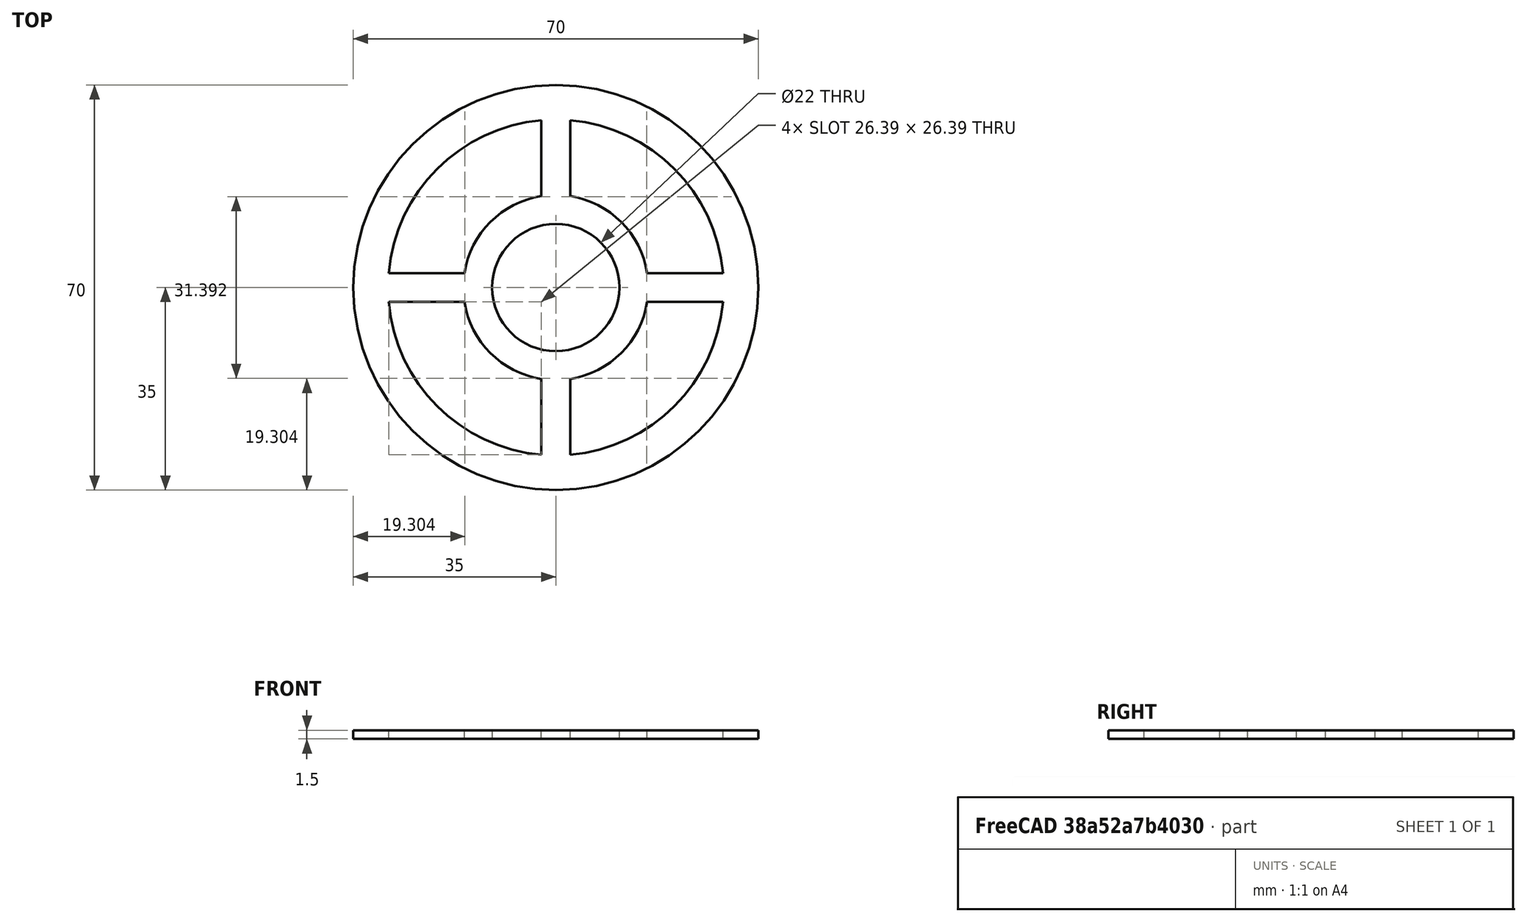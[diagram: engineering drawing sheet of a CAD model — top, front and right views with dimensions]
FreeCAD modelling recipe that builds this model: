
FCSTD DOCUMENT  (FreeCAD 0.14R3700 (Git))
Label: BR_PCB_bas
License: CC-BY 3.0
LicenseURL: http://creativecommons.org/licenses/by/3.0/
objects: Sketcher::SketchObject×1, Part::Extrusion×1, Part::Feature×1
note: 3 computed .brp shape members not serialized (recipe doc carries the construction recipe); baked Part::Feature solids carry a one-line shape summary decoded from their .brp

FEATURE [Sketcher::SketchObject] Sketch  label="PCB_bas"
  sketch-geometry (18):
    g0: Circle CenterX=0 CenterY=0 CenterZ=0 NormalX=0 NormalY=0 NormalZ=1 Radius=35
    g1: Circle CenterX=0 CenterY=0 CenterZ=0 NormalX=0 NormalY=0 NormalZ=1 Radius=11
    g2: ArcOfCircle CenterX=0 CenterY=0 CenterZ=0 NormalX=0 NormalY=0 NormalZ=1 Radius=16 StartAngle=1.72769 EndAngle=2.9847
    g3: ArcOfCircle CenterX=0 CenterY=0 CenterZ=0 NormalX=0 NormalY=0 NormalZ=1 Radius=29 StartAngle=1.65711 EndAngle=3.05528
    g4: LineSegment StartX=-28.892 StartY=2.5 StartZ=0 EndX=-15.8035 EndY=2.5 EndZ=0
    g5: LineSegment StartX=-2.5 StartY=28.892 StartZ=0 EndX=-2.5 EndY=15.8035 EndZ=0
    g6: ArcOfCircle CenterX=0 CenterY=0 CenterZ=0 NormalX=0 NormalY=0 NormalZ=1 Radius=16 StartAngle=0.156893 EndAngle=1.4139
    g7: ArcOfCircle CenterX=0 CenterY=0 CenterZ=0 NormalX=0 NormalY=0 NormalZ=1 Radius=29 StartAngle=0.086314 EndAngle=1.48448
    g8: ArcOfCircle CenterX=0 CenterY=0 CenterZ=0 NormalX=0 NormalY=0 NormalZ=1 Radius=16 StartAngle=4.86928 EndAngle=6.12629
    g9: ArcOfCircle CenterX=0 CenterY=0 CenterZ=0 NormalX=0 NormalY=0 NormalZ=1 Radius=29 StartAngle=4.7987 EndAngle=6.19687
    g10: ArcOfCircle CenterX=0 CenterY=0 CenterZ=0 NormalX=0 NormalY=0 NormalZ=1 Radius=16 StartAngle=3.29849 EndAngle=4.5555
    g11: ArcOfCircle CenterX=0 CenterY=0 CenterZ=0 NormalX=0 NormalY=0 NormalZ=1 Radius=29 StartAngle=3.22791 EndAngle=4.62607
    g12: LineSegment StartX=2.5 StartY=15.8035 StartZ=0 EndX=2.5 EndY=28.892 EndZ=0
    g13: LineSegment StartX=15.8035 StartY=2.5 StartZ=0 EndX=28.892 EndY=2.5 EndZ=0
    g14: LineSegment StartX=15.8035 StartY=-2.5 StartZ=0 EndX=28.892 EndY=-2.5 EndZ=0
    g15: LineSegment StartX=2.5 StartY=-15.8035 StartZ=0 EndX=2.5 EndY=-28.892 EndZ=0
    g16: LineSegment StartX=-2.5 StartY=-15.8035 StartZ=0 EndX=-2.5 EndY=-28.892 EndZ=0
    g17: LineSegment StartX=-15.8035 StartY=-2.5 StartZ=0 EndX=-28.892 EndY=-2.5 EndZ=0
  constraints (48):
    c: Coincident(g0,g-1)
    c: Radius(g0) = 35
    c: Coincident(g1,g-1)
    c: Radius(g1) = 11
    c: Coincident(g2,g-1)
    c: Coincident(g3,g-1)
    c: Coincident(g4,g2)
    c: Coincident(g4,g3)
    c: Parallel(g4,g-1)
    c: Coincident(g5,g3)
    c: Coincident(g5,g2)
    c: Parallel(g5,g-2)
    c: Coincident(g6,g-1)
    c: Coincident(g7,g-1)
    c: Coincident(g8,g-1)
    c: Coincident(g9,g-1)
    c: Coincident(g10,g-1)
    c: Coincident(g12,g6)
    c: Coincident(g12,g7)
    c: Coincident(g13,g6)
    c: Coincident(g13,g7)
    c: Coincident(g14,g8)
    c: Coincident(g14,g9)
    c: Coincident(g15,g8)
    c: Coincident(g15,g9)
    c: Coincident(g16,g10)
    c: Coincident(g16,g11)
    c: Coincident(g17,g10)
    c: Coincident(g17,g11)
    c: Parallel(g-2,g12)
    c: Parallel(g13,g-1)
    c: Parallel(g14,g-1)
    c: Parallel(g15,g-2)
    c: Parallel(g16,g-2)
    c: Parallel(g17,g-1)
    c: Symmetric(g11,g3,g-1)
    c: Symmetric(g2,g6,g-2)
    c: DistanceY(g-1,g11) = -2.5
    c: DistanceX(g-1,g3) = -2.5
    c: Coincident(g11,g-1)
    c: Symmetric(g3,g7,g-2)
    c: Symmetric(g10,g2,g-1)
    c: Symmetric(g2,g10,g-1)
    c: Symmetric(g11,g9,g-2)
    c: Symmetric(g10,g8,g-2)
    c: Symmetric(g6,g8,g-1)
    c: Radius(g11) = 29
    c: Radius(g2) = 16
FEATURE [Part::Extrusion] Extrude
  Base = -> Sketch
  Dir = (0,0,1.5)
  Solid = true
FEATURE [Part::Feature] Extrude001  label="PCB_Bas"
  shape: bbox 70 x 70 x 1.5 mm, 20 faces (baked)
